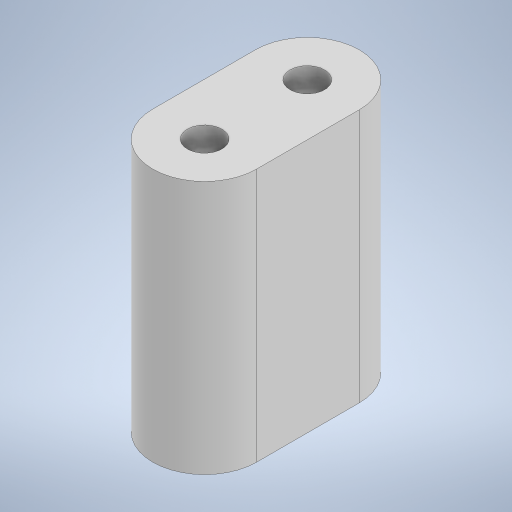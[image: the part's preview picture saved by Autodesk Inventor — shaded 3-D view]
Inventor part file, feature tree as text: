
AUTODESK INVENTOR PART (.ipt)
format: ipt  version: 2023 (Build 270158000, 158)  size: 209,408 bytes
history: native  units: in
note: dims shown in document units (in); Inventor stores cm internally (conversion verified against a paired STEP export)
features: extrude x1, sketch x1
ambient origin geometry x8: Origin, YZ Plane, XZ Plane, XY Plane, X Axis, Y Axis, Z Axis, Center Point
bodies: Solid1 (feature_tree)
feature tree (2):
  extrude  "Extrusion1"  Depth=0.3504in
  sketch  "Sketch1"  dims[d0=0.1181in d1=0.3504in d2=0.1181in d3=0.3543in d4=0.3543in d5=0.8661in d6=0.0in]
